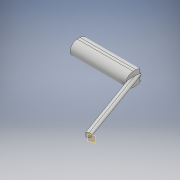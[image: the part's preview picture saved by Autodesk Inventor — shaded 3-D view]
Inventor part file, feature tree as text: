
AUTODESK INVENTOR PART (.ipt)
format: ipt  version: 2018.1 (Build 221171000, 171)  size: 142,848 bytes
history: native  units: mm
features: extrude x3, sketch x3, fillet x2, other x1
ambient origin geometry x8: Origin, YZ Plane, XZ Plane, XY Plane, X Axis, Y Axis, Z Axis, Center Point
bodies: Solide1 (feature_tree)
feature tree (9):
  extrude  "Extrusion1"  Depth=200.0mm
  fillet  "Congé1"  Radius=60.0mm
  other  "Plan de construction6"
  extrude  "Extrusion3"  Depth=100.0mm
  extrude  "Extrusion4"  Depth=30.0mm
  fillet  "Congé2"  Radius=50.0mm
  sketch  "Esquisse1"
  sketch  "Esquisse5"
  sketch  "Esquisse6"
